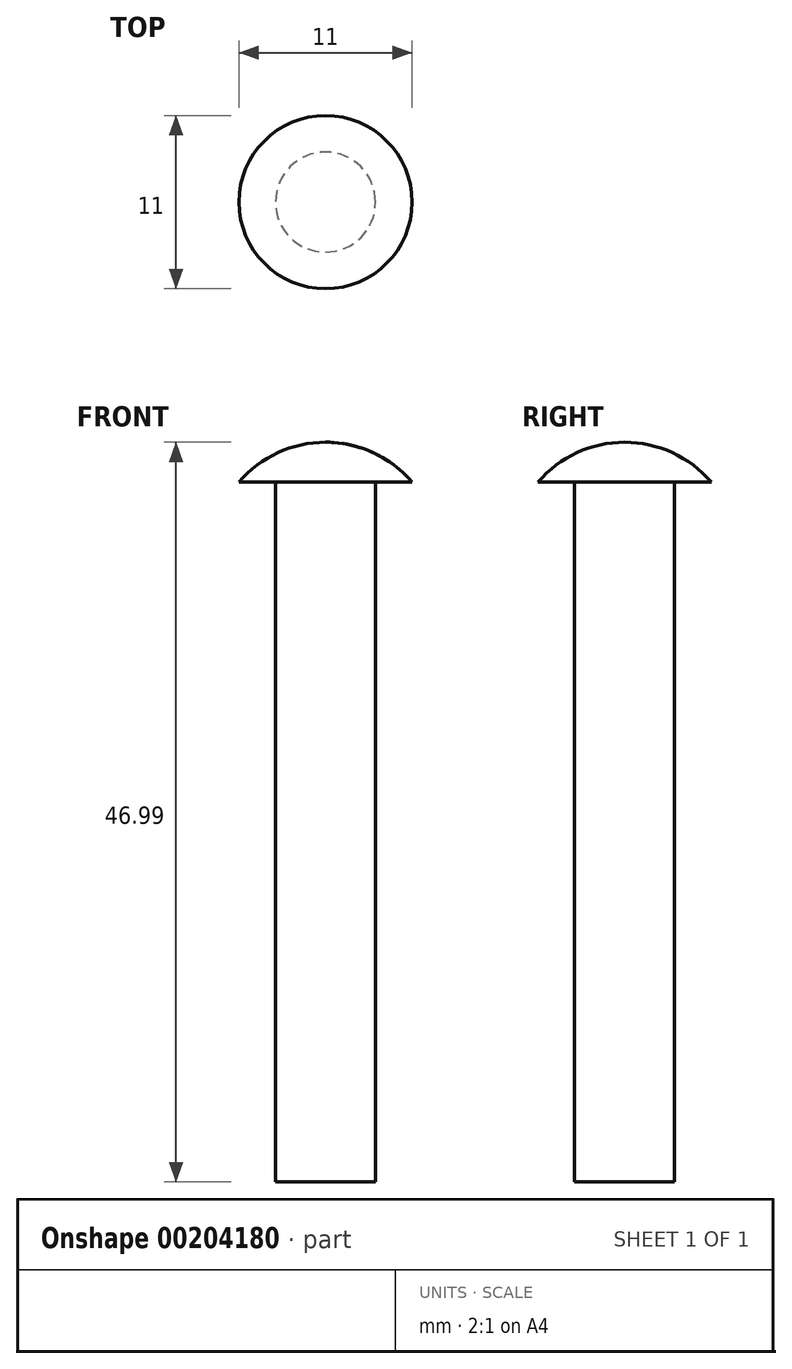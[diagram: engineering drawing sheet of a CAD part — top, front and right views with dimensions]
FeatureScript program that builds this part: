
annotation { "Feature Type Name" : "Feature", "Feature Type Description" : "" }
export const myFeature = defineFeature(function(context is Context, id is Id, definition is map)
    precondition{}
    {
        {
            var Q0;
            Q0=qCreatedBy(makeId("Front.planeOp"),FACE);
            var sketch = newSketch(context, id + "F0", { "sketchPlane" : qUnion([Q0])});
            skLineSegment(sketch, "E0", {"start": v(0, 0) * mm, "end": v(3.18, 0) * mm});
            skLineSegment(sketch, "E1", {"start": v(3.18, 0) * mm, "end": v(3.18, 44.45) * mm});
            skLineSegment(sketch, "E2", {"start": v(3.18, 44.45) * mm, "end": v(5.5, 44.45) * mm});
            skArc(sketch, "E3", {"start": v(5.5, 44.45) * mm, "mid": v(3.03, 46.32) * mm, "end": v(0, 47) * mm});
            skLineSegment(sketch, "E4", {"start": v(0, 47) * mm, "end": v(0, 0) * mm});
            skSolve(sketch);
        }
        {
            var Q0;
            Q0 = qSketchRegion(id + "F0", true);
            var Q1;
            Q1=sQuery(id+"F0.wireOp",EDGE,"E4");
            revolve(context, id + "F1", {"entities" : qUnion([Q0]), "axis" : qUnion([Q1]), "revolveType" : RevolveType.FULL});
        }
    });
